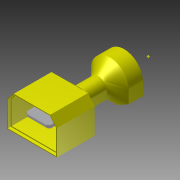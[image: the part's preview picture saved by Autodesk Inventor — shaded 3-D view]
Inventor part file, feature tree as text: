
AUTODESK INVENTOR PART (.ipt)
format: ipt  version: 2011 (Build 150239000, 239)  size: 223,744 bytes
history: native  units: in
note: dims shown in document units (in); Inventor stores cm internally (conversion verified against a paired STEP export)
features: other x4, plane x2, imported_body x1, sketch x1
ambient origin geometry x8: Origin, YZ Plane, XZ Plane, XY Plane, X Axis, Y Axis, Z Axis, Center Point
bodies: Solid1 (feature_tree)
feature tree (8):
  imported_body  "Base1"
  sketch  "Sketch1"  dims[d0=0.125in d1=0.25in]
  other  "Work Point2"
  other  "Work Point3"
  plane  "Work Plane1"
  other  "Work Axis1"
  plane  "Work Plane2"
  other  "Work Axis2"
